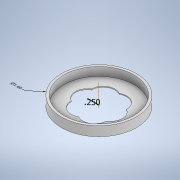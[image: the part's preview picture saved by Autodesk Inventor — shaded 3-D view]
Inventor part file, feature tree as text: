
AUTODESK INVENTOR PART (.ipt)
format: ipt  version: 2020 (Build 240168000, 168)  size: 134,656 bytes
history: native  units: in
note: dims shown in document units (in); Inventor stores cm internally (conversion verified against a paired STEP export)
features: sketch x4, other x3, extrude x3, pattern_circular x1
ambient origin geometry x8: Origin, YZ Plane, XZ Plane, XY Plane, X Axis, Y Axis, Z Axis, Center Point
bodies: Solid1 (feature_tree)
feature tree (11):
  other  "Annotations"
  extrude  "Extrusion1"  Depth=0.2in TaperAngle=0.0deg
  extrude  "Extrusion2"  Depth=0.18in TaperAngle=0.0deg
  sketch  "Sketch3"  dims[d6=0.25in d7=0.18in d8=0.0in d9=2.3622in d10=360.0deg]
  other  "Work Axis1"
  extrude  "Extrusion3"  Depth=0.18in TaperAngle=0.0deg
  pattern_circular  "Circular Pattern1"  Count=6 Angle=360.0deg
  sketch  "Sketch4"  dims[d14=0.25in d12=0.2656in d13=1.6in]
  sketch  "Sketch1"  dims[d0=1.6in d1=0.2in d2=0.0in]
  sketch  "Sketch2"  dims[d3=1.5in d4=0.18in d5=0.0in]
  other  "Diameter Dimension 1"
